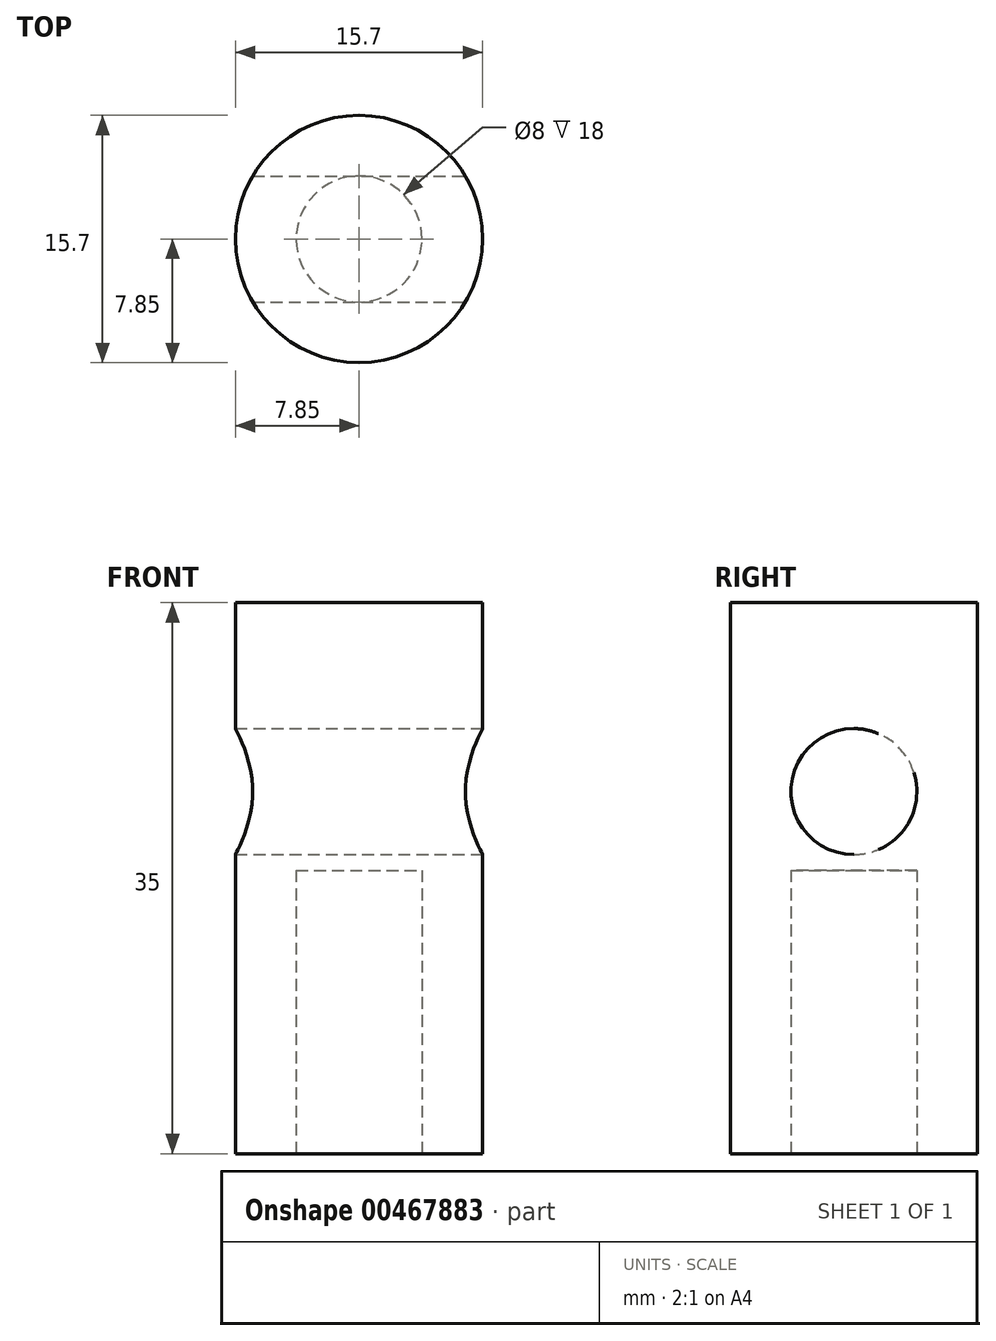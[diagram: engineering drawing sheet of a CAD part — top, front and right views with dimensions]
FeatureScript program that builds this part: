
annotation { "Feature Type Name" : "Feature", "Feature Type Description" : "" }
export const myFeature = defineFeature(function(context is Context, id is Id, definition is map)
    precondition{}
    {
        {
            var Q0;
            Q0=qCreatedBy(makeId("Top.planeOp"),FACE);
            var sketch = newSketch(context, id + "F0", { "sketchPlane" : qUnion([Q0])});
            skCircle(sketch, "E0", {"center": v(0, 0) * mm, "radius": 7.85 * mm});
            skSolve(sketch);
        }
        {
            var Q0;
            Q0=makeQuery(id+"F0.imprint","IMPRINT",FACE,{"disambiguationData":[TD([[makeQuery(id+"F0.imprint","IMPRINT",EDGE,{"derivedFrom":sQuery(id+"F0.wireOp",EDGE,"E0")}),1.0]])]});
            extrude(context, id + "F1", {"entities" : qUnion([Q0]), "depth" : 35 * mm});
        }
        {
            var Q0;
            Q0=qCreatedBy(makeId("Right.planeOp"),FACE);
            var sketch = newSketch(context, id + "F2", { "sketchPlane" : qUnion([Q0])});
            skCircle(sketch, "E1", {"center": v(0, 23) * mm, "radius": 4 * mm});
            skSolve(sketch);
        }
        {
            var Q0;
            Q0 = qSketchRegion(id + "F2", true);
            extrude(context, id + "F3", {"entities" : qUnion([Q0]), "operationType" : NewBodyOperationType.REMOVE, "endBound" : BoundingType.SYMMETRIC, "oppositeDirection" : true, "depth" : 25 * mm});
        }
        {
            var Q0;
            Q0=makeQuery(id+"F1.opExtrude","CAP_FACE",FACE,{"disambiguationData":[OSD([sQuery(id+"F0.wireOp",EDGE,"E0")])],"isStart":true});
            var sketch = newSketch(context, id + "F4", { "sketchPlane" : qUnion([Q0])});
            skCircle(sketch, "E2", {"center": v(0, 0) * mm, "radius": 4 * mm});
            skSolve(sketch);
        }
        {
            var Q0;
            Q0 = qSketchRegion(id + "F4", true);
            extrude(context, id + "F5", {"entities" : qUnion([Q0]), "operationType" : NewBodyOperationType.REMOVE, "oppositeDirection" : true, "depth" : 18 * mm});
        }
    });
